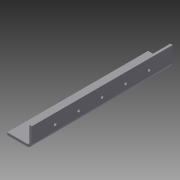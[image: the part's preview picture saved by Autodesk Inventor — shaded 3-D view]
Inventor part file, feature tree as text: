
AUTODESK INVENTOR PART (.ipt)
format: ipt  version: 2015 SP1 (Build 190203100, 203)  size: 136,192 bytes
history: native  units: in
note: dims shown in document units (in); Inventor stores cm internally (conversion verified against a paired STEP export)
features: sheet_metal_op x4, sketch x4, other x3, hole x2
ambient origin geometry x8: Origin, YZ Plane, XZ Plane, XY Plane, X Axis, Y Axis, Z Axis, Center Point
bodies: Solid1 (feature_tree)
feature tree (13):
  other  "<userpath>\Documents\2015 Offseason Chassis\West Coast Chassis Fall 2015\rivet(rv).xlsx"
  sheet_metal_op  "Face1"
  sheet_metal_op  "Flange1"
  hole  "Hole1"  [1 undecoded]
  hole  "Hole2"  [1 undecoded]
  sketch  "Sketch1"  dims[d0=1.0in d1=7.1in]
  other  "Plate1"
  sketch  "Sketch2"  dims[d2=0.12in d3=0.12in]
  other  "Plate2"
  sheet_metal_op  "Bend1"
  sheet_metal_op  "Corner1"
  sketch  "Sketch3"  dims[d4=0.06in]
  sketch  "Sketch4"  dims[d5=0.24in d6=0.12in d7=1.0in d8=90.0deg d9=0.12in d10=0.48in d11=0.12in d12=0.12in d13=0.5in d14=0.1406in d15=0.75in d16=0.375in d17=0.25in d18=0.5635in d19=0.12in d20=0.8108in d21=0.5in d22=0.1406in d23=0.75in d24=0.375in d25=0.25in d26=0.5635in d27=0.12in d28=0.8108in]
note: 2 required parameter values undecoded (feature->parameter linkage not recoverable at this tier; creation-order binding heuristic only, values carry confidence <= 0.55)
